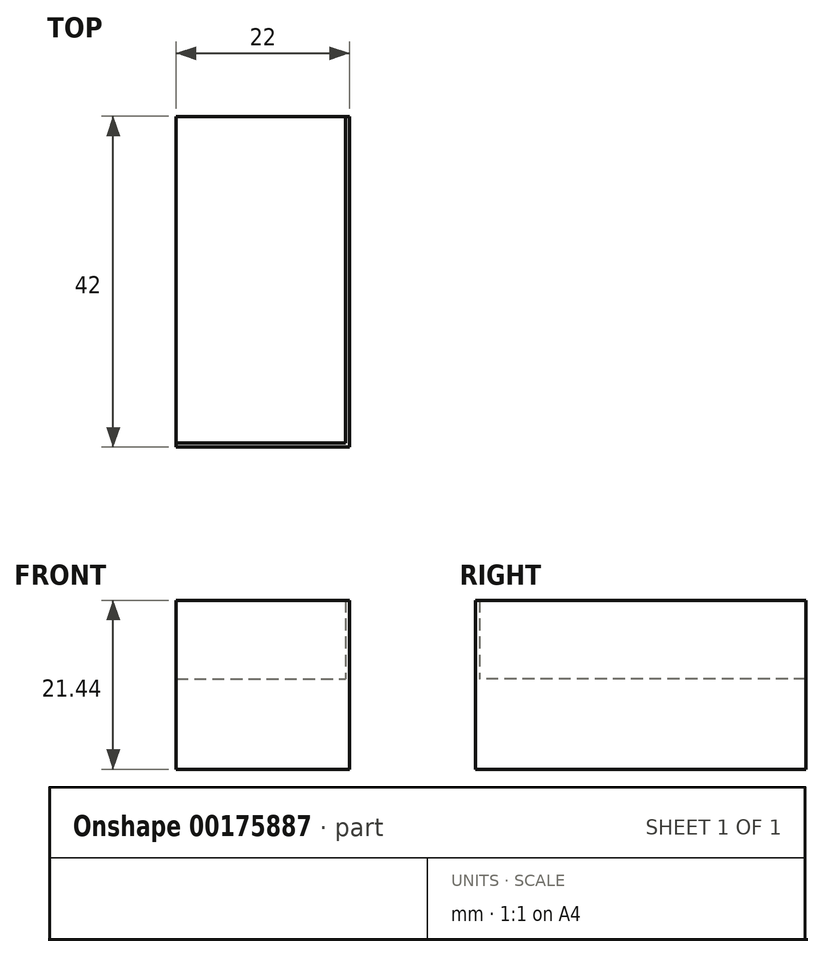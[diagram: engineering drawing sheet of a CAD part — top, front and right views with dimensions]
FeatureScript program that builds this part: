
annotation { "Feature Type Name" : "Feature", "Feature Type Description" : "" }
export const myFeature = defineFeature(function(context is Context, id is Id, definition is map)
    precondition{}
    {
        {
            var Q0;
            Q0=qCreatedBy(makeId("Top.planeOp"),FACE);
            var sketch = newSketch(context, id + "F0", { "sketchPlane" : qUnion([Q0])});
            skLineSegment(sketch, "E0.bottom", {"start": v(-17.23, 34.59) * mm, "end": v(4.77, 34.59) * mm});
            skLineSegment(sketch, "E0.top", {"start": v(-17.23, -7.41) * mm, "end": v(4.77, -7.41) * mm});
            skLineSegment(sketch, "E0.left", {"start": v(-17.23, 34.59) * mm, "end": v(-17.23, -7.41) * mm});
            skLineSegment(sketch, "E0.right", {"start": v(4.77, 34.59) * mm, "end": v(4.77, -7.41) * mm});
            skSolve(sketch);
        }
        {
            var Q0;
            Q0=makeQuery(id+"F0.imprint","IMPRINT",FACE,{"disambiguationData":[TD([[makeQuery(id+"F0.imprint","IMPRINT",EDGE,{"derivedFrom":sQuery(id+"F0.wireOp",EDGE,"E0.bottom")}),-1.0]])]});
            extrude(context, id + "F1", {"entities" : qUnion([Q0]), "depth" : 11.44 * mm});
        }
        {
            var Q0;
            Q0=makeQuery(id+"F1.opExtrude","SWEPT_FACE",FACE,{"disambiguationData":[OSD([sQuery(id+"F0.wireOp",EDGE,"E0.top")])]});
            var sketch = newSketch(context, id + "F2", { "sketchPlane" : qUnion([Q0])});
            skLineSegment(sketch, "E1", {"start": v(4.77, 11.44) * mm, "end": v(4.77, 21.44) * mm});
            skLineSegment(sketch, "E2", {"start": v(4.77, 21.44) * mm, "end": v(4.27, 21.44) * mm});
            skLineSegment(sketch, "E3", {"start": v(4.27, 21.44) * mm, "end": v(4.27, 11.44) * mm});
            skLineSegment(sketch, "E4", {"start": v(4.27, 11.44) * mm, "end": v(4.77, 11.44) * mm});
            skSolve(sketch);
        }
        {
            var Q0;
            Q0=makeQuery(id+"F2.imprint","IMPRINT",FACE,{"disambiguationData":[TD([[makeQuery(id+"F2.imprint","IMPRINT",EDGE,{"derivedFrom":sQuery(id+"F2.wireOp",EDGE,"E1")}),1.0]])]});
            extrude(context, id + "F3", {"entities" : qUnion([Q0]), "operationType" : NewBodyOperationType.ADD, "oppositeDirection" : true, "depth" : 42 * mm});
        }
        {
            var Q0;
            Q0=makeQuery(id+"F3.opExtrude","SWEPT_FACE",FACE,{"disambiguationData":[OSD([sQuery(id+"F2.wireOp",EDGE,"E3")])]});
            var sketch = newSketch(context, id + "F4", { "sketchPlane" : qUnion([Q0])});
            skLineSegment(sketch, "E5.bottom", {"start": v(6.91, 21.44) * mm, "end": v(7.41, 21.44) * mm});
            skLineSegment(sketch, "E5.top", {"start": v(6.91, 11.44) * mm, "end": v(7.41, 11.44) * mm});
            skLineSegment(sketch, "E5.left", {"start": v(6.91, 21.44) * mm, "end": v(6.91, 11.44) * mm});
            skLineSegment(sketch, "E5.right", {"start": v(7.41, 21.44) * mm, "end": v(7.41, 11.44) * mm});
            skSolve(sketch);
        }
        {
            var Q0;
            Q0 = qSketchRegion(id + "F4", true);
            extrude(context, id + "F5", {"entities" : qUnion([Q0]), "operationType" : NewBodyOperationType.ADD, "depth" : 21.5 * mm});
        }
    });
